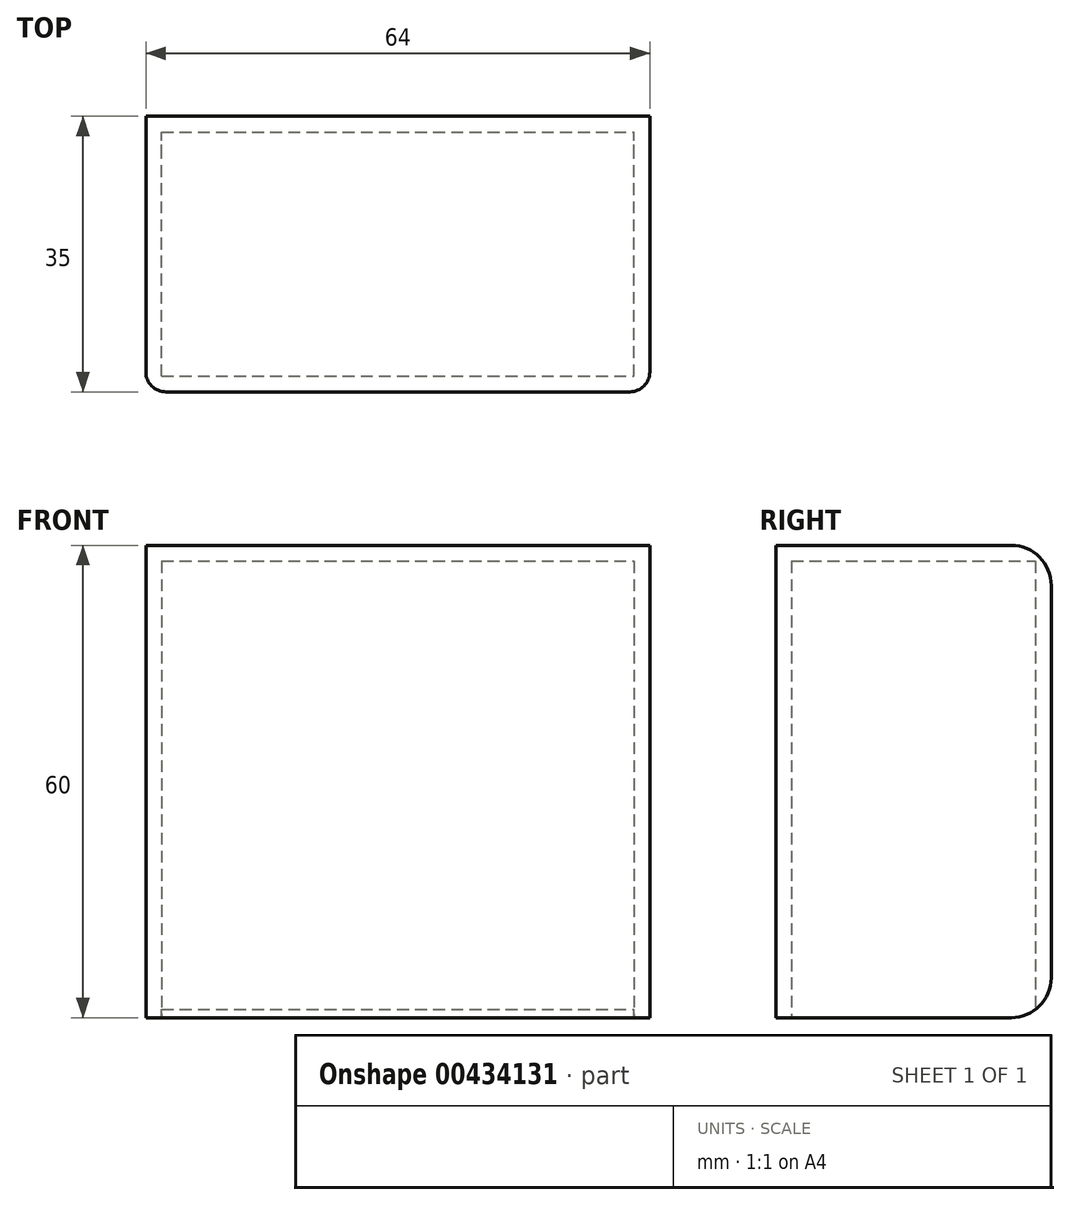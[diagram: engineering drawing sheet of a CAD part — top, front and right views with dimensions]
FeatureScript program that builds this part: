
annotation { "Feature Type Name" : "Feature", "Feature Type Description" : "" }
export const myFeature = defineFeature(function(context is Context, id is Id, definition is map)
    precondition{}
    {
        {
            var Q0;
            Q0=qCreatedBy(makeId("Front.planeOp"),FACE);
            var sketch = newSketch(context, id + "F0", { "sketchPlane" : qUnion([Q0])});
            skLineSegment(sketch, "E0.bottom", {"start": v(-33.74, 49.68) * mm, "end": v(30.26, 49.68) * mm});
            skLineSegment(sketch, "E0.top", {"start": v(-33.74, -10.32) * mm, "end": v(30.26, -10.32) * mm});
            skLineSegment(sketch, "E0.left", {"start": v(-33.74, 49.68) * mm, "end": v(-33.74, -10.32) * mm});
            skLineSegment(sketch, "E0.right", {"start": v(30.26, 49.68) * mm, "end": v(30.26, -10.32) * mm});
            skSolve(sketch);
        }
        {
            var Q0;
            Q0 = qSketchRegion(id + "F0", true);
            extrude(context, id + "F1", {"entities" : qUnion([Q0]), "depth" : 35 * mm});
        }
        {
            var Q0;
            Q0=makeQuery(id+"F1.opExtrude","SWEPT_FACE",FACE,{"disambiguationData":[OSD([sQuery(id+"F0.wireOp",EDGE,"E0.top")])]});
            shell(context, id + "F2", {"entities" : qUnion([Q0]), "thickness" : 2 * mm});
        }
        {
            var Q0;
            Q0=makeQuery(id+"F1.opExtrude","CAP_EDGE",EDGE,{"disambiguationData":[OSD([sQuery(id+"F0.wireOp",EDGE,"E0.bottom")])],"isStart":true});
            fillet(context, id + "F3", {"entities" : qUnion([Q0]), "radius" : 5.08 * mm, "tangentPropagation" : true, "allowEdgeOverflow" : false});
        }
        {
            var Q0;
            Q0=makeQuery(id+"F1.opExtrude","CAP_EDGE",EDGE,{"disambiguationData":[OSD([sQuery(id+"F0.wireOp",EDGE,"E0.top")])],"isStart":true});
            fillet(context, id + "F4", {"entities" : qUnion([Q0]), "radius" : 5.08 * mm, "tangentPropagation" : true, "allowEdgeOverflow" : false});
        }
        {
            var Q0;
            Q0=makeQuery(id+"F1.opExtrude","CAP_EDGE",EDGE,{"disambiguationData":[OSD([sQuery(id+"F0.wireOp",EDGE,"E0.left")])],"isStart":false});
            var Q1;
            Q1=makeQuery(id+"F1.opExtrude","CAP_EDGE",EDGE,{"disambiguationData":[OSD([sQuery(id+"F0.wireOp",EDGE,"E0.right")])],"isStart":false});
            fillet(context, id + "F5", {"entities" : qUnion([Q0, Q1]), "radius" : 2.54 * mm, "tangentPropagation" : true, "allowEdgeOverflow" : false});
        }
    });
